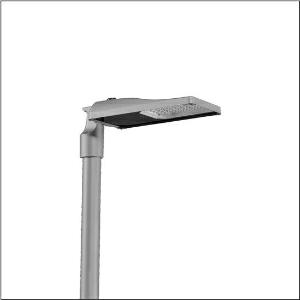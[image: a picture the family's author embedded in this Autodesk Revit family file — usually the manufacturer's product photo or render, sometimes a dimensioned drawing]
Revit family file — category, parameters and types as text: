
# Revit family: streetlight_sl_31_mini___st1_0a_5xh6d31s08ga_35d4
name_source: partatom
category: Lighting Fixtures
units: mm (PartAtom-declared; Revit-internal decimal feet)

## family parameters
Cut with Voids When Loaded = No
Host = Face
Light Source = No
Part Type = Normal
Room Calculation Point = No
Round Connector Dimension = Use Diameter
Shared = No

## types (1)
- --- (1 x LED, 5880 lm, 39.3 W, 3000K)
    Apparent Load = 39 VA
    CIE Flux Codes = 37 72 97 100 100
    Color Rendering = 70
    Color Temperature = 3000K
    Default Elevation = 1800 mm
    Description = Streetlight SL 31 mini D4i, Desk-Remote mast luminaire for post-top, side-entry; light control with lens of PMMA; light distribution: ST1.0a, direct asymmetric distribution, for standard-compliant lighting for roads and squares; LED: luminous flux: 5.880lm, light colour: 730, colour temperature: 3000K; luminous efficacy: 149,6lm/W; control: pre-setting: logarithmic dimming characteristic, flexible luminous flux parameterisation, time-dependent luminous flux control, constant luminous flux control, power reduction, intelligent temperature release in ECG and LED module, overheat protection; luminaire housing, of diecast aluminium, SITECO metallic grey (DB 702S), corrosivity category C5 high according to DIN EN ISO 12944; cover of toughened safety glass, transparent, opened without tools; mast flange of diecast aluminium, SITECO metallic grey (DB 702S), spigot size: 76/60mm, mast flange included unmounted; with cable H07RN-F 2x 1.5mm², cable length: 6,5m, connection cable pre-assembled; mains connection: 220..240V, AC, 50/60Hz; power consumption (at start of service life): 39,3W / (at end of service life): 40,7W / (with reduced operation 50%): 18,1W; protection rating (complete): IP66; insulation class (complete): insulation class II (safety insulation); impact resistance: IK10; certification: CE, ENEC, ENEC+, VDE, UKCA, ZD4i; permissible operating ambient temperature for outdoor applications: -40..+50°C; packaging unit: 1 piece

Light Distribution: ST1.0a
    Height = 76 mm
    Lamp = 1 x LED
    Lamp Light Flux = 5880 lm
    Lamp Power = 39.3 W
    Lamp count = 1
    Length = 547 mm
    Luminous efficacy = 150 lm/W
    Manufacturer = Siteco
    ModVariant = No
    Model = 5XH6D31S08GA
    Mounting Place = Pole
    Mounting Type = Pole top
    Number of Poles = 1
    OnlyDefault = Yes
    Power Factor = 1
    Product Name = Streetlight SL 31 mini | ST1.0a
    Product group = mast luminaire | pylon top
    ProductGroupID = 6100
    Protection Class = Protection class II
    Protection Degree = IP 66
    RLX_Detail_Level = 1
    RLX_Emergency_Light_Flux = 0 lm
    RLX_Emergency_Type = 0
    RLX_Emergency_Type_DB = No
    RlxData = <blob elided: 39581 chars, md5=fe257c44>
    Socket = socket
    Standby Power = 0 W
    System Light Flux = 5880 lm
    System Power = 39 W
    Type Comments = factory setting: luminous flux: 100 % | dim-lin: 254 | 798 mA
    Type Image = l_1300330.jpg
    URL = http://relux.com
    VarID = @adj_062267
    Voltage = 0 V
    Weight = 0.00 kg
    Width = 265 mm

## geometry (parser evidence)
native form markers: Blend x4, Sweep x9
no freeform markers — native parametric forms only
